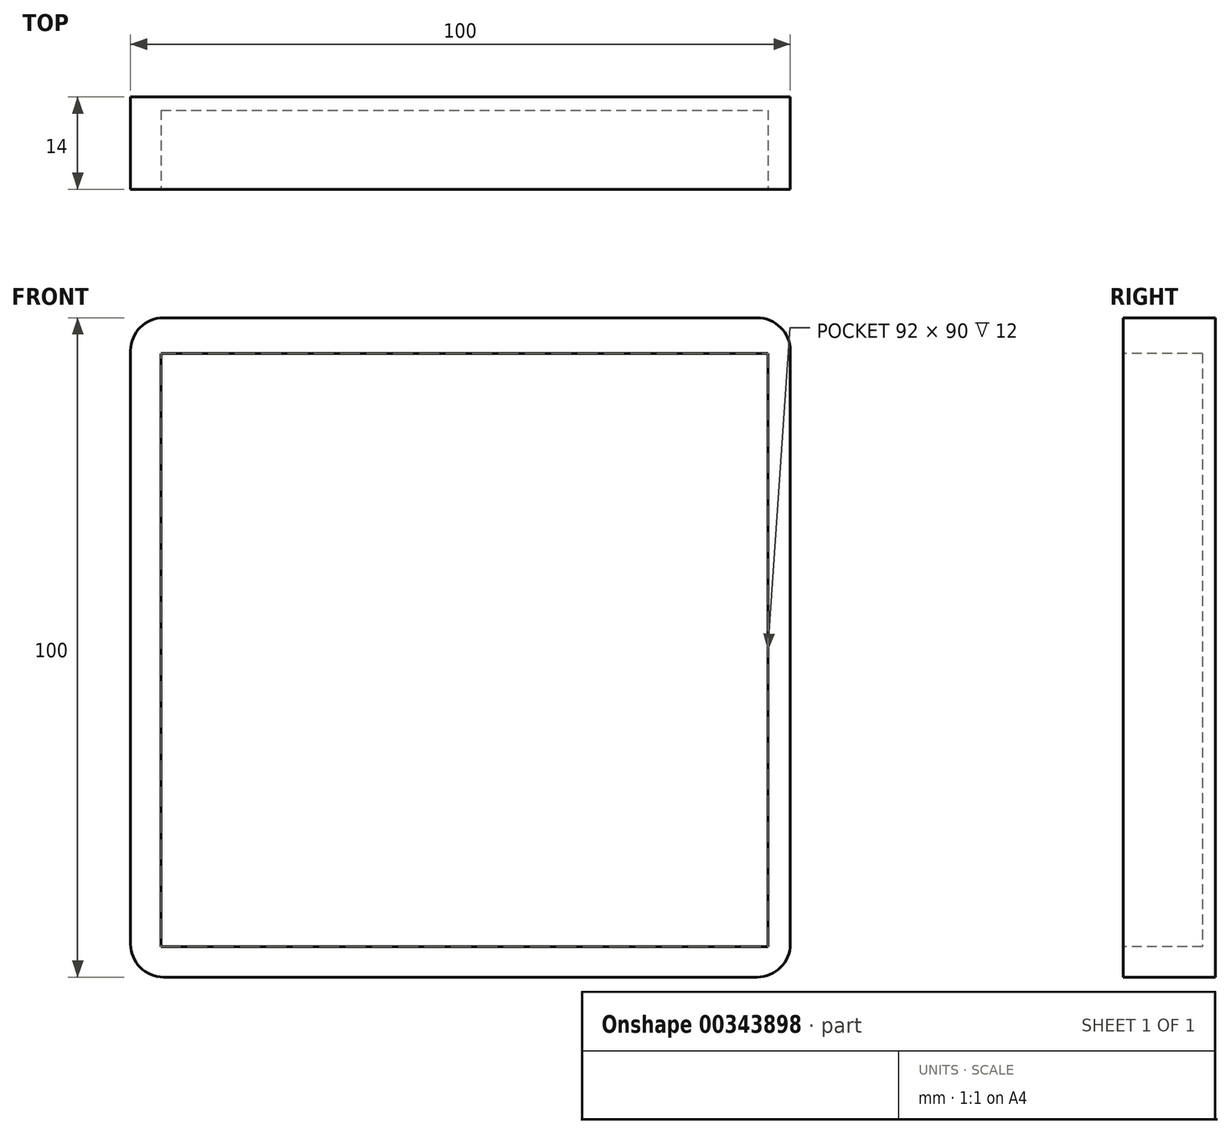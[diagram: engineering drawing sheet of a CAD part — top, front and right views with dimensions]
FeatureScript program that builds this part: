
annotation { "Feature Type Name" : "Feature", "Feature Type Description" : "" }
export const myFeature = defineFeature(function(context is Context, id is Id, definition is map)
    precondition{}
    {
        {
            var Q0;
            Q0=qCreatedBy(makeId("Front.planeOp"),FACE);
            var sketch = newSketch(context, id + "F0", { "sketchPlane" : qUnion([Q0])});
            skLineSegment(sketch, "E0.bottom", {"start": v(55.4, -38.42) * mm, "end": v(-44.6, -38.42) * mm});
            skLineSegment(sketch, "E0.top", {"start": v(55.4, 61.58) * mm, "end": v(-44.6, 61.58) * mm});
            skLineSegment(sketch, "E0.left", {"start": v(55.4, -38.42) * mm, "end": v(55.4, 61.58) * mm});
            skLineSegment(sketch, "E0.right", {"start": v(-44.6, -38.42) * mm, "end": v(-44.6, 61.58) * mm});
            skSolve(sketch);
        }
        {
            var Q0;
            Q0=makeQuery(id+"F0.imprint","IMPRINT",FACE,{"disambiguationData":[TD([[makeQuery(id+"F0.imprint","IMPRINT",EDGE,{"derivedFrom":sQuery(id+"F0.wireOp",EDGE,"E0.bottom")}),-1.0]])]});
            extrude(context, id + "F1", {"entities" : qUnion([Q0]), "depth" : 14 * mm});
        }
        {
            var Q0;
            Q0=makeQuery(id+"F1.opExtrude","CAP_FACE",FACE,{"disambiguationData":[OSD([sQuery(id+"F0.wireOp",EDGE,"E0.bottom"),sQuery(id+"F0.wireOp",EDGE,"E0.top"),sQuery(id+"F0.wireOp",EDGE,"E0.left"),sQuery(id+"F0.wireOp",EDGE,"E0.right")])],"isStart":false});
            var sketch = newSketch(context, id + "F2", { "sketchPlane" : qUnion([Q0])});
            skLineSegment(sketch, "E1.bottom", {"start": v(-39.98, 56.18) * mm, "end": v(52.02, 56.18) * mm});
            skLineSegment(sketch, "E1.top", {"start": v(-39.98, -33.82) * mm, "end": v(52.02, -33.82) * mm});
            skLineSegment(sketch, "E1.left", {"start": v(-39.98, 56.18) * mm, "end": v(-39.98, -33.82) * mm});
            skLineSegment(sketch, "E1.right", {"start": v(52.02, 56.18) * mm, "end": v(52.02, -33.82) * mm});
            skSolve(sketch);
        }
        {
            var Q0;
            Q0=makeQuery(id+"F2.imprint","IMPRINT",FACE,{"disambiguationData":[TD([[makeQuery(id+"F2.imprint","IMPRINT",EDGE,{"derivedFrom":sQuery(id+"F2.wireOp",EDGE,"E1.bottom")}),-1.0]])]});
            extrude(context, id + "F3", {"entities" : qUnion([Q0]), "operationType" : NewBodyOperationType.REMOVE, "oppositeDirection" : true, "depth" : 12 * mm});
        }
        {
            var Q0;
            Q0=makeQuery(id+"F1.opExtrude","SWEPT_EDGE",EDGE,{"disambiguationData":[OSD([sQuery(id+"F0.wireOp",EDGE,"E0.bottom"),sQuery(id+"F0.wireOp",EDGE,"E0.right")])]});
            var Q1;
            Q1=makeQuery(id+"F1.opExtrude","SWEPT_EDGE",EDGE,{"disambiguationData":[OSD([sQuery(id+"F0.wireOp",EDGE,"E0.bottom"),sQuery(id+"F0.wireOp",EDGE,"E0.left")])]});
            var Q2;
            Q2=makeQuery(id+"F1.opExtrude","SWEPT_EDGE",EDGE,{"disambiguationData":[OSD([sQuery(id+"F0.wireOp",EDGE,"E0.top"),sQuery(id+"F0.wireOp",EDGE,"E0.left")])]});
            var Q3;
            Q3=makeQuery(id+"F1.opExtrude","SWEPT_EDGE",EDGE,{"disambiguationData":[OSD([sQuery(id+"F0.wireOp",EDGE,"E0.top"),sQuery(id+"F0.wireOp",EDGE,"E0.right")])]});
            fillet(context, id + "F4", {"entities" : qUnion([Q0, Q1, Q2, Q3]), "radius" : 5 * mm, "tangentPropagation" : true, "allowEdgeOverflow" : false});
        }
    });
